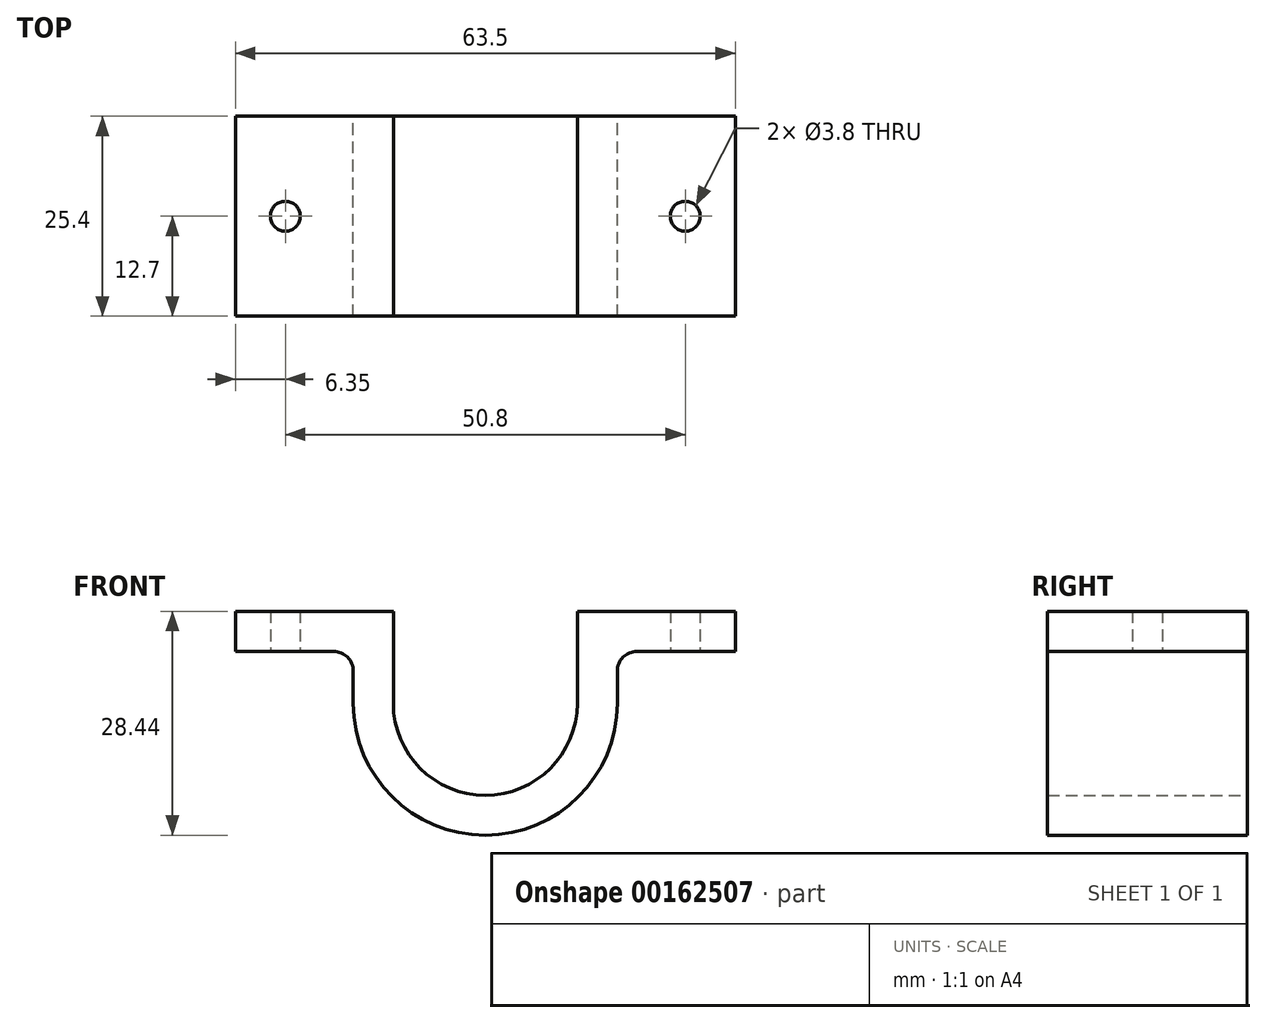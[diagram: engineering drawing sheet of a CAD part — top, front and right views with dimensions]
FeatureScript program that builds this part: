
annotation { "Feature Type Name" : "Feature", "Feature Type Description" : "" }
export const myFeature = defineFeature(function(context is Context, id is Id, definition is map)
    precondition{}
    {
        {
            var Q0;
            Q0=qCreatedBy(makeId("Front.planeOp"),FACE);
            var sketch = newSketch(context, id + "F0", { "sketchPlane" : qUnion([Q0])});
            skArc(sketch, "E0", {"start": v(-11.68, 0) * mm, "mid": v(0, -11.68) * mm, "end": v(11.68, 0) * mm});
            skLineSegment(sketch, "E1", {"start": v(-31.75, 11.68) * mm, "end": v(-11.68, 11.68) * mm});
            skLineSegment(sketch, "E2", {"start": v(11.68, 11.68) * mm, "end": v(31.75, 11.68) * mm});
            skLineSegment(sketch, "E3", {"start": v(-11.68, 0) * mm, "end": v(-11.68, 11.68) * mm});
            skLineSegment(sketch, "E4", {"start": v(11.68, 11.68) * mm, "end": v(11.68, 0) * mm});
            skLineSegment(sketch, "E5.0", {"start": v(16.76, 6.6) * mm, "end": v(31.75, 6.6) * mm});
            skLineSegment(sketch, "E5.1", {"start": v(-31.75, 6.6) * mm, "end": v(-16.76, 6.6) * mm});
            skLineSegment(sketch, "E5.2", {"start": v(-16.76, 0) * mm, "end": v(-16.76, 6.6) * mm});
            skArc(sketch, "E5.3", {"start": v(-16.76, 0) * mm, "mid": v(0, -16.76) * mm, "end": v(16.76, 0) * mm});
            skLineSegment(sketch, "E5.4", {"start": v(16.76, 6.6) * mm, "end": v(16.76, 0) * mm});
            skLineSegment(sketch, "E6", {"start": v(-31.75, 6.6) * mm, "end": v(-31.75, 11.68) * mm});
            skLineSegment(sketch, "E7", {"start": v(31.75, 11.68) * mm, "end": v(31.75, 6.6) * mm});
            skSolve(sketch);
        }
        {
            var Q0;
            Q0 = qSketchRegion(id + "F0", true);
            extrude(context, id + "F1", {"entities" : qUnion([Q0]), "depth" : 25.4 * mm});
        }
        {
            var Q0;
            Q0=makeQuery(id+"F1.opExtrude","SWEPT_FACE",FACE,{"disambiguationData":[OSD([sQuery(id+"F0.wireOp",EDGE,"E5.1")])]});
            var sketch = newSketch(context, id + "F2", { "sketchPlane" : qUnion([Q0])});
            skPoint(sketch, "E8", {"position": v(-25.4, 12.7) * mm});
            skPoint(sketch, "E9", {"position": v(25.4, 12.7) * mm});
            skPoint(sketch, "E10", {"position": v(-31.75, 12.7) * mm});
            skSolve(sketch);
        }
        {
            var Q0;
            Q0=sQuery(id+"F2.wireOp",VERTEX,"E8");
            var Q1;
            Q1=sQuery(id+"F2.wireOp",VERTEX,"E9");
            var Q2;
            Q2=makeQuery(id+"F1.opExtrude","SWEPT_BODY",BODY,{"disambiguationData":[OSD([sQuery(id+"F0.wireOp",EDGE,"E0"),sQuery(id+"F0.wireOp",EDGE,"E1"),sQuery(id+"F0.wireOp",EDGE,"E2"),sQuery(id+"F0.wireOp",EDGE,"E3"),sQuery(id+"F0.wireOp",EDGE,"E4"),sQuery(id+"F0.wireOp",EDGE,"E5.0"),sQuery(id+"F0.wireOp",EDGE,"E5.1"),sQuery(id+"F0.wireOp",EDGE,"E5.2"),sQuery(id+"F0.wireOp",EDGE,"E5.3"),sQuery(id+"F0.wireOp",EDGE,"E5.4"),sQuery(id+"F0.wireOp",EDGE,"E6"),sQuery(id+"F0.wireOp",EDGE,"E7")])]});
            hole(context, id + "F3", {"style" : HoleStyle.SIMPLE, "endStyle" : HoleEndStyle.BLIND, "standardTappedOrClearance" : lookupTablePath({ "standard" : "ANSI", "fit" : "Normal (ASME)", "size" : "#6", "type" : "Clearance" }), "standardBlindInLast" : lookupTablePath({ "fit" : "Free", "standard" : "ANSI", "size" : "#6", "type" : "Clearance" }), "holeDiameter" : 3.8 * mm, "holeDepth" : 101.6 * mm, "isTappedThrough" : true, "tappedDepth" : 3.96 * mm, "tapClearance" : 3, "locations" : qUnion([Q0, Q1]), "scope" : qUnion([Q2])});
        }
        {
            var Q0;
            Q0=makeQuery(id+"F1.opExtrude","SWEPT_EDGE",EDGE,{"disambiguationData":[OSD([sQuery(id+"F0.wireOp",EDGE,"E5.0"),sQuery(id+"F0.wireOp",EDGE,"E5.4")])]});
            var Q1;
            Q1=makeQuery(id+"F1.opExtrude","SWEPT_EDGE",EDGE,{"disambiguationData":[OSD([sQuery(id+"F0.wireOp",EDGE,"E5.1"),sQuery(id+"F0.wireOp",EDGE,"E5.2")])]});
            fillet(context, id + "F4", {"entities" : qUnion([Q0, Q1]), "radius" : 2.54 * mm, "tangentPropagation" : true, "allowEdgeOverflow" : false});
        }
    });
